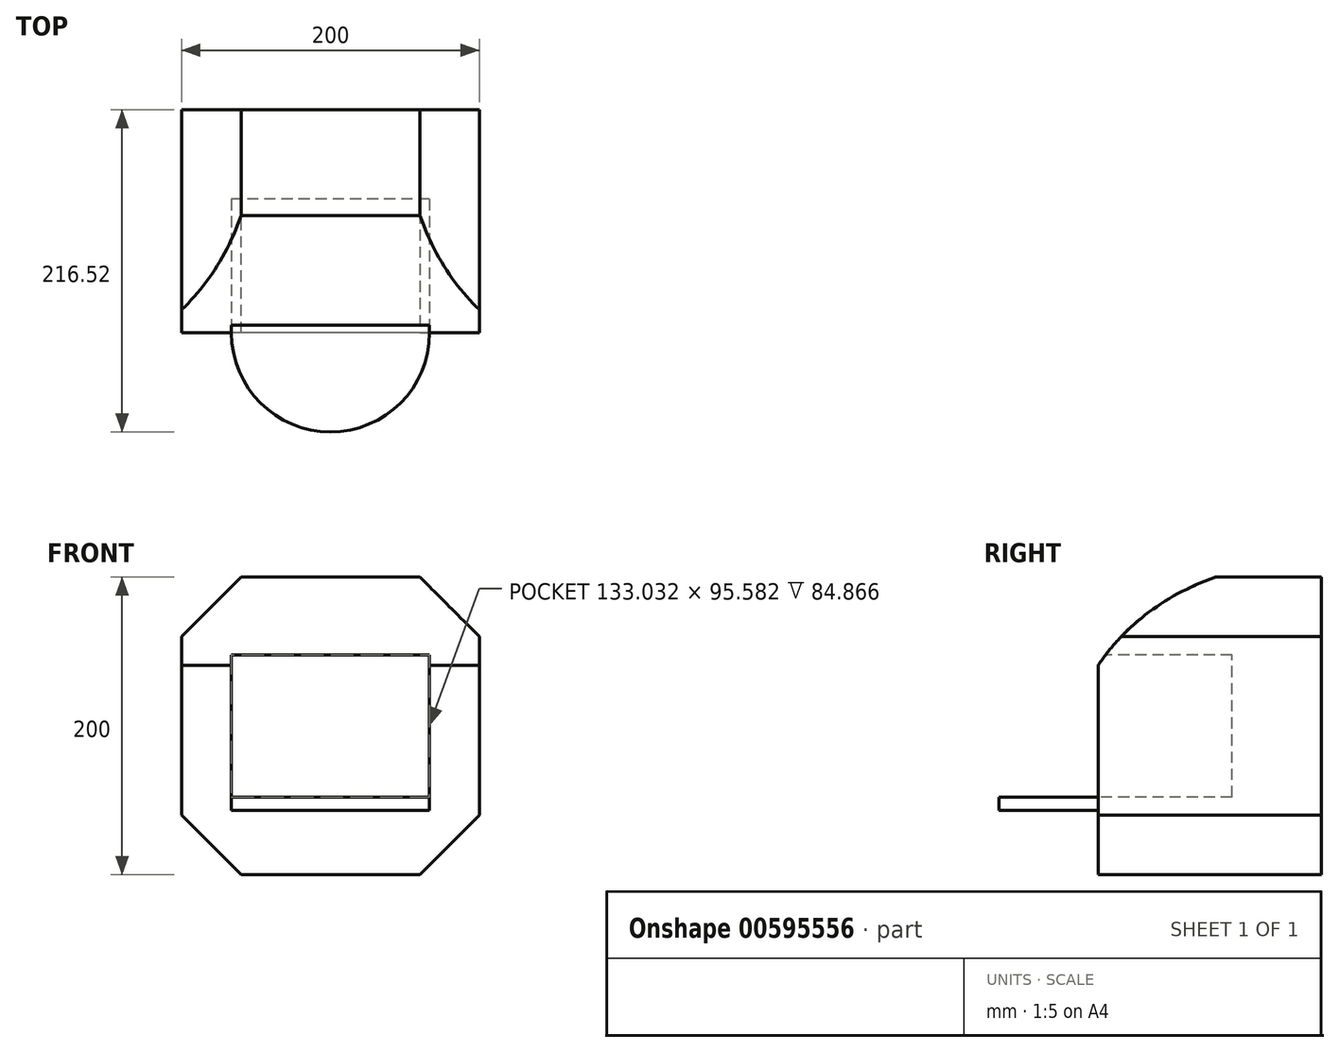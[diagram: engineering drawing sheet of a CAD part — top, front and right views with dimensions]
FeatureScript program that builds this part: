
annotation { "Feature Type Name" : "Feature", "Feature Type Description" : "" }
export const myFeature = defineFeature(function(context is Context, id is Id, definition is map)
    precondition{}
    {
        {
            var Q0;
            Q0=qCreatedBy(makeId("Front.planeOp"),FACE);
            var sketch = newSketch(context, id + "F0", { "sketchPlane" : qUnion([Q0])});
            skLineSegment(sketch, "E0.bottom", {"start": v(100, -100) * mm, "end": v(-100, -100) * mm});
            skLineSegment(sketch, "E0.top", {"start": v(100, 100) * mm, "end": v(-100, 100) * mm});
            skLineSegment(sketch, "E0.left", {"start": v(100, -100) * mm, "end": v(100, 100) * mm});
            skLineSegment(sketch, "E0.right", {"start": v(-100, -100) * mm, "end": v(-100, 100) * mm});
            skPoint(sketch, "E0.middle", {"position": v(0, 0) * mm});
            skSolve(sketch);
        }
        {
            var Q0;
            Q0=makeQuery(id+"F0.imprint","IMPRINT",FACE,{"disambiguationData":[TD([[makeQuery(id+"F0.imprint","IMPRINT",EDGE,{"derivedFrom":sQuery(id+"F0.wireOp",EDGE,"E0.bottom")}),-1.0]])]});
            extrude(context, id + "F1", {"entities" : qUnion([Q0]), "endBound" : BoundingType.SYMMETRIC, "depth" : 150 * mm, "offsetDistance" : 25 * mm});
        }
        {
            var Q0;
            Q0=makeQuery(id+"F1.opExtrude","SWEPT_EDGE",EDGE,{"disambiguationData":[OSD([sQuery(id+"F0.wireOp",EDGE,"E0.top"),sQuery(id+"F0.wireOp",EDGE,"E0.left")])]});
            var Q1;
            Q1=makeQuery(id+"F1.opExtrude","SWEPT_EDGE",EDGE,{"disambiguationData":[OSD([sQuery(id+"F0.wireOp",EDGE,"E0.top"),sQuery(id+"F0.wireOp",EDGE,"E0.right")])]});
            var Q2;
            Q2=makeQuery(id+"F1.opExtrude","SWEPT_EDGE",EDGE,{"disambiguationData":[OSD([sQuery(id+"F0.wireOp",EDGE,"E0.bottom"),sQuery(id+"F0.wireOp",EDGE,"E0.right")])]});
            var Q3;
            Q3=makeQuery(id+"F1.opExtrude","SWEPT_EDGE",EDGE,{"disambiguationData":[OSD([sQuery(id+"F0.wireOp",EDGE,"E0.bottom"),sQuery(id+"F0.wireOp",EDGE,"E0.left")])]});
            chamfer(context, id + "F2", {"entities" : qUnion([Q0, Q1, Q2, Q3]), "width" : 40 * mm, "tangentPropagation" : true});
        }
        {
            var Q0;
            Q0=makeQuery(id+"F1.opExtrude","CAP_FACE",FACE,{"disambiguationData":[OSD([sQuery(id+"F0.wireOp",EDGE,"E0.bottom"),sQuery(id+"F0.wireOp",EDGE,"E0.top"),sQuery(id+"F0.wireOp",EDGE,"E0.left"),sQuery(id+"F0.wireOp",EDGE,"E0.right")])],"isStart":false});
            var sketch = newSketch(context, id + "F3", { "sketchPlane" : qUnion([Q0])});
            skLineSegment(sketch, "E1.bottom", {"start": v(66.52, -47.8) * mm, "end": v(-66.52, -47.8) * mm});
            skLineSegment(sketch, "E1.top", {"start": v(66.52, 47.8) * mm, "end": v(-66.52, 47.8) * mm});
            skLineSegment(sketch, "E1.left", {"start": v(66.52, -47.8) * mm, "end": v(66.52, 47.8) * mm});
            skLineSegment(sketch, "E1.right", {"start": v(-66.52, -47.8) * mm, "end": v(-66.52, 47.8) * mm});
            skPoint(sketch, "E1.middle", {"position": v(0, 0) * mm});
            skSolve(sketch);
        }
        {
            var Q0;
            Q0=makeQuery(id+"F3.imprint","IMPRINT",FACE,{"disambiguationData":[TD([[makeQuery(id+"F3.imprint","IMPRINT",EDGE,{"derivedFrom":sQuery(id+"F3.wireOp",EDGE,"E1.bottom")}),-1.0]])]});
            extrude(context, id + "F4", {"entities" : qUnion([Q0]), "operationType" : NewBodyOperationType.REMOVE, "oppositeDirection" : true, "depth" : 90 * mm, "offsetDistance" : 25 * mm});
        }
        {
            var Q0;
            Q0=makeQuery(id+"F1.opExtrude","SWEPT_FACE",FACE,{"disambiguationData":[OSD([sQuery(id+"F0.wireOp",EDGE,"E0.left")])]});
            var sketch = newSketch(context, id + "F5", { "sketchPlane" : qUnion([Q0])});
            skPoint(sketch, "E2.1.internal.orphan", {"position": v(-207.27, 114.8) * mm});
            skPoint(sketch, "E3.end.orphan", {"position": v(18.77, 114.8) * mm});
            skFitSpline(sketch, "E4", {"points": [v(-88, -22.94) * mm, v(-83.38, 24.5) * mm, v(-30, 83.82) * mm, v(56.33, 114.8) * mm], "startDerivative": vector(-10.21, 171.15) * mm, "endDerivative": vector(239.97, 58.63) * mm});
            skLineSegment(sketch, "E5", {"start": v(56.33, 114.8) * mm, "end": v(-23.41, 159.6) * mm});
            skLineSegment(sketch, "E6", {"start": v(-23.41, 159.6) * mm, "end": v(-86.68, 159.6) * mm});
            skLineSegment(sketch, "E7", {"start": v(-86.68, 159.6) * mm, "end": v(-134.78, 0) * mm});
            skLineSegment(sketch, "E8", {"start": v(-134.78, 0) * mm, "end": v(-95.24, -20.97) * mm});
            skLineSegment(sketch, "E9", {"start": v(-88, -22.94) * mm, "end": v(-95.24, -20.97) * mm});
            skSolve(sketch);
        }
        {
            var Q0;
            {var subQ0=sQuery(id+"F5.wireOp",EDGE,"E5");Q0=makeQuery(id+"F5.imprint","IMPRINT",FACE,{"disambiguationData":[TD([[makeQuery(id+"F5.imprint","IMPRINT",EDGE,{"derivedFrom":subQ0}),1.0]])]});}
            var Q1;
            {var subQ0=sQuery(id+"F5.wireOp",EDGE,"E4");var subQ1=sQuery(id+"F0.wireOp",EDGE,"E0.left");var subQ2=makeQuery(id+"F1.opExtrude","CAP_EDGE",EDGE,{"disambiguationData":[OSD([subQ1])],"isStart":false});var subQ3=makeQuery(id+"F5.imprint","INTERSECT",VERTEX,{"derivedFrom":[subQ2,subQ0]});Q1=makeQuery(id+"F5.imprint","IMPRINT",FACE,{"disambiguationData":[TD([[makeQuery(id+"F5.imprint","IMPRINT",EDGE,{"disambiguationData":[TD([[subQ3,-1.0]])],"derivedFrom":subQ0}),1.0]])]});}
            extrude(context, id + "F6", {"entities" : qUnion([Q0, Q1]), "operationType" : NewBodyOperationType.REMOVE, "oppositeDirection" : true, "depth" : 200.9 * mm, "offsetDistance" : 25 * mm});
        }
        {
            var Q0;
            Q0=makeQuery(id+"F4.boolean.opBoolean","COPY",FACE,{"derivedFrom":makeQuery(id+"F4.opExtrude","SWEPT_FACE",FACE,{"disambiguationData":[OSD([sQuery(id+"F3.wireOp",EDGE,"E1.bottom")])]})});
            var sketch = newSketch(context, id + "F7", { "sketchPlane" : qUnion([Q0])});
            skArc(sketch, "E10", {"start": v(-66.52, -75) * mm, "mid": v(0, -141.52) * mm, "end": v(66.52, -75) * mm});
            skLineSegment(sketch, "E11", {"start": v(-66.52, -75) * mm, "end": v(66.52, -75) * mm});
            skSolve(sketch);
        }
        {
            var Q0;
            Q0=makeQuery(id+"F7.imprint","IMPRINT",FACE,{"disambiguationData":[TD([[makeQuery(id+"F7.imprint","IMPRINT",EDGE,{"derivedFrom":sQuery(id+"F7.wireOp",EDGE,"E10")}),1.0]])]});
            extrude(context, id + "F8", {"entities" : qUnion([Q0]), "operationType" : NewBodyOperationType.ADD, "oppositeDirection" : true, "depth" : 9 * mm, "offsetDistance" : 25 * mm});
        }
    });
